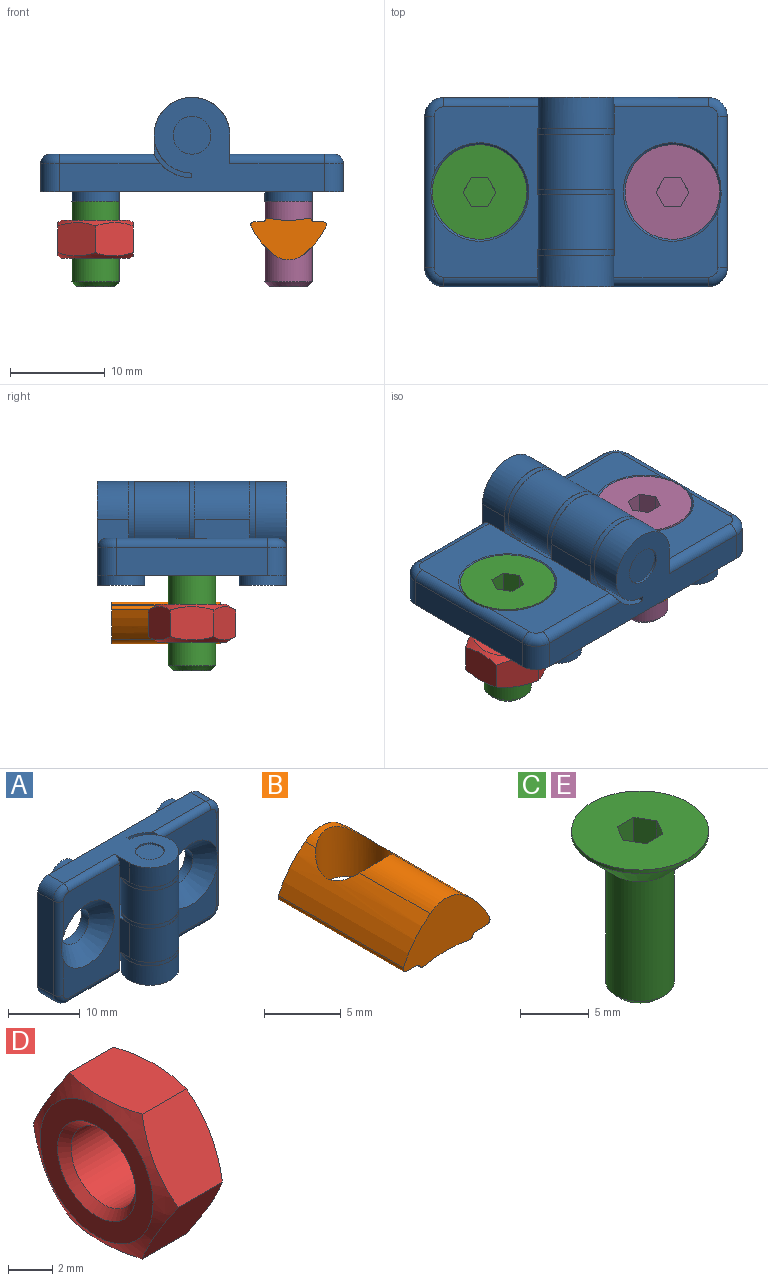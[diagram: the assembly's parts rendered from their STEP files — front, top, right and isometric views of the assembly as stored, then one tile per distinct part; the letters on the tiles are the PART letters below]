
ASSEMBLY  parts=5 mates=4
PART A: 59 faces, bbox 32.3x11x20.3 mm
  f0: cylinder r=4mm len=7.99mm, axis (0,0,1), area 15.1mm2, adj f21,f36
  f1: cylinder r=4mm len=7.99mm, axis (0,0,1), area 15.1mm2, adj f20,f37
  f2: cylinder r=4mm len=7.99mm, axis (0,0,1), area 15.1mm2, adj f19,f38
  f3: cylinder r=4mm len=8mm, axis (0,0,-1), area 62.2mm2, adj f36,f47,f48,f56
  f4: cylinder r=4mm len=8mm, axis (0,0,-1), area 109.3mm2, adj f35,f37,f38,f57
  f5: cylinder r=2.75mm len=5.5mm, axis (0,1,0), area 25.9mm2, adj f9,f58
  f6: cylinder r=2mm len=4mm, axis (0,0,1), area 3.1mm2, adj f39,f47
  f7: cylinder r=2.49mm len=4.99mm, axis (0,1,0), area 15.7mm2, adj f54,f58
  f8: cylinder r=2.49mm len=4.99mm, axis (0,1,0), area 15.7mm2, adj f53,f58
  f9: cone r=3.98mm half-angle=44.4deg, axis (0,-1,0), area 87.3mm2, adj f5,f42,f49
  f10: cylinder r=4mm len=8mm, axis (0,0,1), area 62.2mm2, adj f17,f20,f28,f52
  f11: cylinder r=4mm len=8mm, axis (0,0,1), area 109.3mm2, adj f18,f19,f21,f34
  f12: cylinder r=2.75mm len=5.5mm, axis (0,1,0), area 25.9mm2, adj f15,f58
  f13: cylinder r=2.49mm len=4.99mm, axis (0,1,0), area 15.7mm2, adj f33,f58
  f14: cylinder r=2.49mm len=4.99mm, axis (0,1,0), area 15.7mm2, adj f32,f58
  f15: cone r=3.98mm half-angle=44.4deg, axis (0,-1,0), area 87.3mm2, adj f12,f23,f29
  f16: cylinder r=2mm len=4mm, axis (0,0,-1), area 3.1mm2, adj f40,f52
  f17: plane 3.3x0.5mm, normal (1,0,0), area 1.6mm2, adj f10,f20,f52,f55
  f18: plane 5.8x0.5mm, normal (1,0,0), area 2.9mm2, adj f11,f19,f21,f55
  f19: plane 8.5x8.03mm, normal (0,0,1), area 2.8mm2, adj f2,f11,f18,f23,f34,f55
  f20: plane 8.5x8.03mm, normal (0,0,-1), area 2.8mm2, adj f1,f10,f17,f23,f28,f55
  f21: plane 8.5x8.03mm, normal (0,0,-1), area 2.8mm2, adj f0,f11,f18,f23,f34,f55
  f22: torus R=1mm, axis (0,-1,0), area 4mm2, adj f23,f27,f29,f30
  f23: plane 18x11mm, normal (0,-1,0), area 113.4mm2, adj f15,f19,f20,f21,f22,f24,f26,f27
  f24: torus R=1mm, axis (0,-1,0), area 4mm2, adj f23,f25,f26,f29
  f25: cylinder r=2mm len=3mm, axis (0,1,0), area 9.4mm2, adj f24,f31,f47,f58
  f26: cylinder r=1mm len=10.65mm, axis (1,0,0), area 16.2mm2, adj f23,f24,f47,f55
  f27: cylinder r=1mm len=10mm, axis (1,0,0), area 15.7mm2, adj f22,f23,f28,f52
  f28: plane 3.3x3mm, normal (-1,0,0), area 6.8mm2, adj f10,f20,f23,f27,f52
  f29: cylinder r=1mm len=16mm, axis (0,0,1), area 24.4mm2, adj f15,f22,f23,f24,f31
  f30: cylinder r=2mm len=3mm, axis (0,1,0), area 9.4mm2, adj f22,f31,f52,f58
  f31: plane 16x3mm, normal (-1,0,0), area 48mm2, adj f25,f29,f30,f58
  f32: plane 4.99x4.99mm, normal (0,1,0), area 19.6mm2, adj f14
  f33: plane 4.99x4.99mm, normal (0,1,0), area 19.6mm2, adj f13
  f34: plane 5.8x2mm, normal (-1,0,0), area 11.6mm2, adj f11,f19,f21,f23
  f35: plane 5.8x0.5mm, normal (-1,0,0), area 2.9mm2, adj f4,f37,f38,f55
  f36: plane 8.5x8.03mm, normal (0,0,1), area 2.8mm2, adj f0,f3,f42,f48,f55,f56
  f37: plane 8.5x8.03mm, normal (0,0,1), area 2.8mm2, adj f1,f4,f35,f42,f55,f57
  f38: plane 8.5x8.03mm, normal (0,0,-1), area 2.8mm2, adj f2,f4,f35,f42,f55,f57
  f39: plane 4x4mm, normal (0,0,-1), area 12.6mm2, adj f6
  f40: plane 4x4mm, normal (0,0,1), area 12.6mm2, adj f16
  f41: torus R=1mm, axis (0,-1,0), area 4mm2, adj f42,f46,f49,f50
  f42: plane 18x11mm, normal (0,-1,0), area 113.4mm2, adj f9,f36,f37,f38,f41,f43,f45,f46
  f43: torus R=1mm, axis (0,-1,0), area 4mm2, adj f42,f44,f45,f49
  f44: cylinder r=2mm len=3mm, axis (0,1,0), area 9.4mm2, adj f43,f51,f52,f58
  f45: cylinder r=1mm len=10.65mm, axis (-1,0,0), area 16.2mm2, adj f42,f43,f52,f55
  f46: cylinder r=1mm len=10mm, axis (-1,0,0), area 15.7mm2, adj f41,f42,f47,f48
  f47: plane 28x10mm, normal (0,0,-1), area 117.6mm2, adj f3,f6,f25,f26,f46,f48,f50,f55
  f48: plane 3.3x3mm, normal (1,0,0), area 6.8mm2, adj f3,f36,f42,f46,f47
  f49: cylinder r=1mm len=16mm, axis (0,0,-1), area 24.4mm2, adj f9,f41,f42,f43,f51
  f50: cylinder r=2mm len=3mm, axis (0,1,0), area 9.4mm2, adj f41,f47,f51,f58
  f51: plane 16x3mm, normal (1,0,0), area 48mm2, adj f44,f49,f50,f58
  f52: plane 28x10mm, normal (0,0,1), area 117.6mm2, adj f10,f16,f17,f27,f28,f30,f44,f45
  f53: plane 4.99x4.99mm, normal (0,1,0), area 19.6mm2, adj f8
  f54: plane 4.99x4.99mm, normal (0,1,0), area 19.6mm2, adj f7
  f55: cylinder r=4.5mm len=20mm, axis (0,0,-1), area 107.7mm2, adj f17,f18,f19,f20,f21,f23,f26,f35
  f56: plane 3.3x0.5mm, normal (-1,0,0), area 1.7mm2, adj f3,f36,f47,f55
  f57: plane 5.8x2mm, normal (1,0,0), area 11.6mm2, adj f4,f37,f38,f42
  f58: plane 32x20mm, normal (0,1,0), area 510.8mm2, adj f5,f7,f8,f12,f13,f14,f25,f30
PART B: 23 faces, bbox 8x11.5x4.4 mm
  f0: cylinder r=2.5mm len=5mm, axis (0,0,-1), area 55.9mm2, adj f1,f2,f3,f4,f5,f6,f7,f8
  f1: cylinder r=8mm len=11.5mm, axis (0,1,0), area 42mm2, adj f0,f2,f14,f15,f21,f22
  f2: cylinder r=2.5mm len=3.01mm, axis (0,1,0), area 2.4mm2, adj f0,f1,f13,f21
  f3: cylinder r=0.3mm len=11.5mm, axis (0,1,0), area 4.2mm2, adj f0,f4,f10,f11,f21,f22
  f4: cylinder r=0.3mm len=2.5mm, axis (0,1,0), area 0.8mm2, adj f0,f3,f5,f21
  f5: plane 1.75x0.03mm, normal (0,0,-1), area 0.1mm2, adj f0,f4,f6,f21
  f6: cylinder r=9.9mm len=4.27mm, axis (0,1,0), area 4.7mm2, adj f0,f5,f7,f21
  f7: plane 1.75x0.03mm, normal (0,0,-1), area 0.1mm2, adj f0,f6,f8,f21
  f8: cylinder r=0.3mm len=2.5mm, axis (0,1,0), area 0.8mm2, adj f0,f7,f17,f21
  f9: plane 7.25x0.03mm, normal (0,0,-1), area 0.2mm2, adj f0,f10,f20,f22
  f10: cylinder r=0.3mm len=8mm, axis (0,1,0), area 2.8mm2, adj f0,f3,f9,f22
  f11: plane 11.5x0.98mm, normal (0,0,-1), area 11.3mm2, adj f3,f12,f21,f22
  f12: cylinder r=0.3mm len=11.5mm, axis (0,1,0), area 6.9mm2, adj f11,f13,f21,f22
  f13: cylinder r=8mm len=11.5mm, axis (0,1,0), area 42.2mm2, adj f0,f2,f12,f14,f21,f22
  f14: cylinder r=2.5mm len=6.52mm, axis (0,1,0), area 20.2mm2, adj f0,f1,f13,f22
  f15: cylinder r=0.3mm len=11.5mm, axis (0,1,0), area 6.9mm2, adj f1,f16,f21,f22
  f16: plane 11.5x0.95mm, normal (0,0,-1), area 10.9mm2, adj f15,f17,f21,f22
  f17: cylinder r=0.3mm len=11.5mm, axis (0,1,0), area 4.2mm2, adj f0,f8,f16,f18,f21,f22
  f18: cylinder r=0.3mm len=8mm, axis (0,1,0), area 2.8mm2, adj f0,f17,f19,f22
  f19: plane 7.25x0.03mm, normal (0,0,-1), area 0.2mm2, adj f0,f18,f20,f22
  f20: cylinder r=9.9mm len=7.2mm, axis (0,1,0), area 28.4mm2, adj f0,f9,f19,f22
  f21: plane 8x4.4mm, normal (0,1,0), area 23.8mm2, adj f1,f2,f3,f4,f5,f6,f7,f8
  f22: plane 8x4.4mm, normal (0,-1,0), area 23.8mm2, adj f1,f3,f9,f10,f11,f12,f13,f14
PART C: 13 faces, bbox 10x10x14 mm
  f0: cylinder r=5mm len=10mm, axis (0,0,-1), area 9.4mm2, adj f1,f9
  f1: cone r=2.5mm half-angle=45deg, axis (0,0,1), area 83.3mm2, adj f0,f2
  f2: cylinder r=2.5mm len=10.71mm, axis (0,0,-1), area 168.2mm2, adj f1,f3
  f3: cone r=1.25mm half-angle=45deg, axis (0,0,1), area 9.8mm2, adj f2,f12
  f4: plane 3.3x1.5mm, normal (0.87,0.5,0), area 5.7mm2, adj f6,f8,f9,f11
  f5: plane 3.3x1.5mm, normal (-0.87,-0.5,0), area 5.7mm2, adj f6,f7,f9,f10
  f6: plane 3.46x3mm, normal (0,0,1), area 7.8mm2, adj f4,f5,f7,f8,f10,f11
  f7: plane 3.3x1.5mm, normal (-0.87,0.5,0), area 5.7mm2, adj f5,f6,f9,f11
  f8: plane 3.3x1.5mm, normal (0.87,-0.5,0), area 5.7mm2, adj f4,f6,f9,f10
  f9: plane 10x10mm, normal (0,0,1), area 70.7mm2, adj f0,f4,f5,f7,f8,f10,f11
  f10: plane 3.3x1.73mm, normal (0,-1,0), area 5.7mm2, adj f5,f6,f8,f9
  f11: plane 3.3x1.73mm, normal (0,1,0), area 5.7mm2, adj f4,f6,f7,f9
  f12: plane 4.02x4.02mm, normal (0,0,-1), area 12.7mm2, adj f3
PART D: 13 faces, bbox 4.4x9.6x9.6 mm
  f0: plane 4x3.54mm, normal (0,0.87,0.5), area 15.2mm2, adj f1,f8,f10,f12
  f1: cone r=3.6mm half-angle=60deg, axis (1,0,0), area 17.6mm2, adj f0,f2,f3,f9,f10,f11,f12
  f2: plane 5x3.92mm, normal (0,0,-1), area 15.2mm2, adj f1,f8,f10,f11
  f3: plane 4x3.54mm, normal (0,-0.87,0.5), area 15.2mm2, adj f1,f8,f11,f12
  f4: cone r=2.07mm half-angle=45deg, axis (1,0,0), area 8.8mm2, adj f5,f7
  f5: cylinder r=2.07mm len=4.13mm, axis (-1,0,0), area 40.7mm2, adj f4,f6
  f6: cone r=2.5mm half-angle=45deg, axis (-1,0,0), area 8.8mm2, adj f5,f9
  f7: plane 7.2x7.2mm, normal (1,0,0), area 21.1mm2, adj f4,f8
  f8: cone r=4.8mm half-angle=60deg, axis (-1,0,0), area 17mm2, adj f0,f2,f3,f7,f10,f11,f12
  f9: plane 7.2x7.2mm, normal (-1,0,0), area 21.1mm2, adj f1,f6
  f10: plane 4x3.54mm, normal (0,0.87,-0.5), area 15.2mm2, adj f0,f1,f2,f8
  f11: plane 4x3.54mm, normal (0,-0.87,-0.5), area 15.2mm2, adj f1,f2,f3,f8
  f12: plane 4.62x3.54mm, normal (0,0,1), area 15.2mm2, adj f0,f1,f3,f8
PART E: same geometry as C
PLACE A rot(axis=(-1,0,0),90deg) t=(121.61,-63.26,10.85)mm
PLACE B rot(axis=(1,0,0),180deg) t=(142.01,-63.26,7.68)mm
PLACE C t=(121.61,-63.26,12.05)mm
PLACE D rot(axis=(0,-1,0),90deg) t=(121.61,-63.26,3.85)mm
PLACE E t=(142.01,-63.26,12.05)mm
MATE fastened D.f1 <-> A.f12  axis (0,0,1) through (121.61,-63.26,7.85)mm
MATE fastened E.f0 <-> A.f5  axis (0,0,1) through (142.01,-63.26,14.85)mm
MATE fastened C.f0 <-> A.f12  axis (0,0,1) through (121.61,-63.26,14.85)mm
MATE fastened B.f0 <-> A.f5  axis (0,0,1) through (142.01,-63.26,8.08)mm
